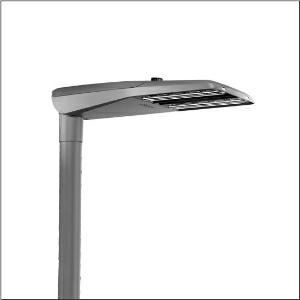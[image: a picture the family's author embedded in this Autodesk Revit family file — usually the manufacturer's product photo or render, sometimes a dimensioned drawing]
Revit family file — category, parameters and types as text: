
# Revit family: streetlight_sl_11_iq_midi___st1_2a_5xc3a41u08me_4bff
name_source: partatom
category: Lighting Fixtures
units: mm (PartAtom-declared; Revit-internal decimal feet)

## family parameters
Cut with Voids When Loaded = No
Host = Face
Light Source = No
Part Type = Normal
Room Calculation Point = No
Round Connector Dimension = Use Diameter
Shared = No

## types (1)
- --- (1 x LED, 18900 lm, 122.6 W, 4000K)
    Apparent Load = 123 VA
    CIE Flux Codes = 32 70 96 100 100
    Color Rendering = 70
    Color Temperature = 4000K
    Default Elevation = 1800 mm
    Description = Streetlight SL 11 iQ midi, mast luminaire, primary light control with 3 zone facetted reflector, of plastic, silver coated, highly specular, primary optical cover: cover, of PMMA, transparent, light distribution: ST1.2a, light emission: direct distribution, primary light characteristic: asymmetric, installation type: post-top, side-entry, LED, High Power LED, rated luminous flux: 18.900lm, luminous efficacy: 154lm/W, light colour: 740, colour temperature: 4000K, control: presetting dimming logarithmic, Street-Remote, Auto-Match, Temp-Guard, Lumen-Switch, Night-Set, Smart-Wire, Light-Fading, Desk-Remote (wireless, voltage-free reading and setting of iQ features in the workshop via application-optimized NFC function/RFID function), optimised constant luminous flux control (CLO 2.0), with cable H07RN-F 5x 1.5mm², mains connection: 230..240V, AC, 50/60Hz, connection cable pre-assembled, cable length: 12,5m, start of lifetime: 123W, end of service life: 130W, reduction: 56W, luminaire housing, of diecast aluminium, powder-coated, Siteco® metallic grey (DB 702S), please order mast flange separately, inclination adjustable without tools: 0°, 5°, 10°, 15° (post-top) | 0°, -5°, -10°, -15° (side-entry), sealing non-destructively replaceable, multi-level sealing system, length: 780mm, width: 376mm, height: 118mm, mast flange for spigot size: 42mm (side-entry): 5XC10008XM4, 60/48mm (side-entry/post-top): 5XC10108XM2, 76/60mm (side-entry/post-top): 5XC10108XM1, equipment: Power, Smart Interface below, protection rating (complete): IP66, insulation class (complete): insulation class II (safety insulation), certification: CE, ENEC, VDE, UKCA, impact resistance: IK09, permissible operating ambient temperature for outdoor applications: -25..+50°C, standard-compliant lighting for roads and squares, Environmental Product Declaration (EPD) tested and certified by an independent institute, packaging unit: 1 piece

Light Distribution: ST1.2a
    Height = 118 mm
    Lamp = 1 x LED
    Lamp Light Flux = 18900 lm
    Lamp Power = 122.6 W
    Lamp count = 1
    Length = 780 mm
    Luminous efficacy = 154 lm/W
    Manufacturer = Siteco
    ModVariant = No
    Model = 5XC3A41U08ME
    Number of Poles = 1
    OnlyDefault = Yes
    Power Factor = 1
    Product Name = Streetlight SL 11 iQ midi | ST1.2a
    Product group = mast luminaire | pylon top
    ProductGroupID = 6100
    Protection Class = Protection class II
    Protection Degree = IP 66
    RLX_Detail_Level = 1
    RLX_Emergency_Light_Flux = 0 lm
    RLX_Emergency_Type = 0
    RLX_Emergency_Type_DB = No
    RlxData = <blob elided: 69801 chars, md5=3c34041c>
    Socket = socket
    Standby Power = 0 W
    System Light Flux = 18900 lm
    System Power = 123 W
    Type Comments = factory setting: luminous flux: 100 % | dim-lin: 254 | 552 mA
    Type Image = l_1005968.jpg
    URL = http://relux.com
    VarID = @adj_064409
    Voltage = 0 V
    Weight = 0.00 kg
    Width = 376 mm

## geometry (parser evidence)
native form markers: Blend x4, Sweep x10
no freeform markers — native parametric forms only
